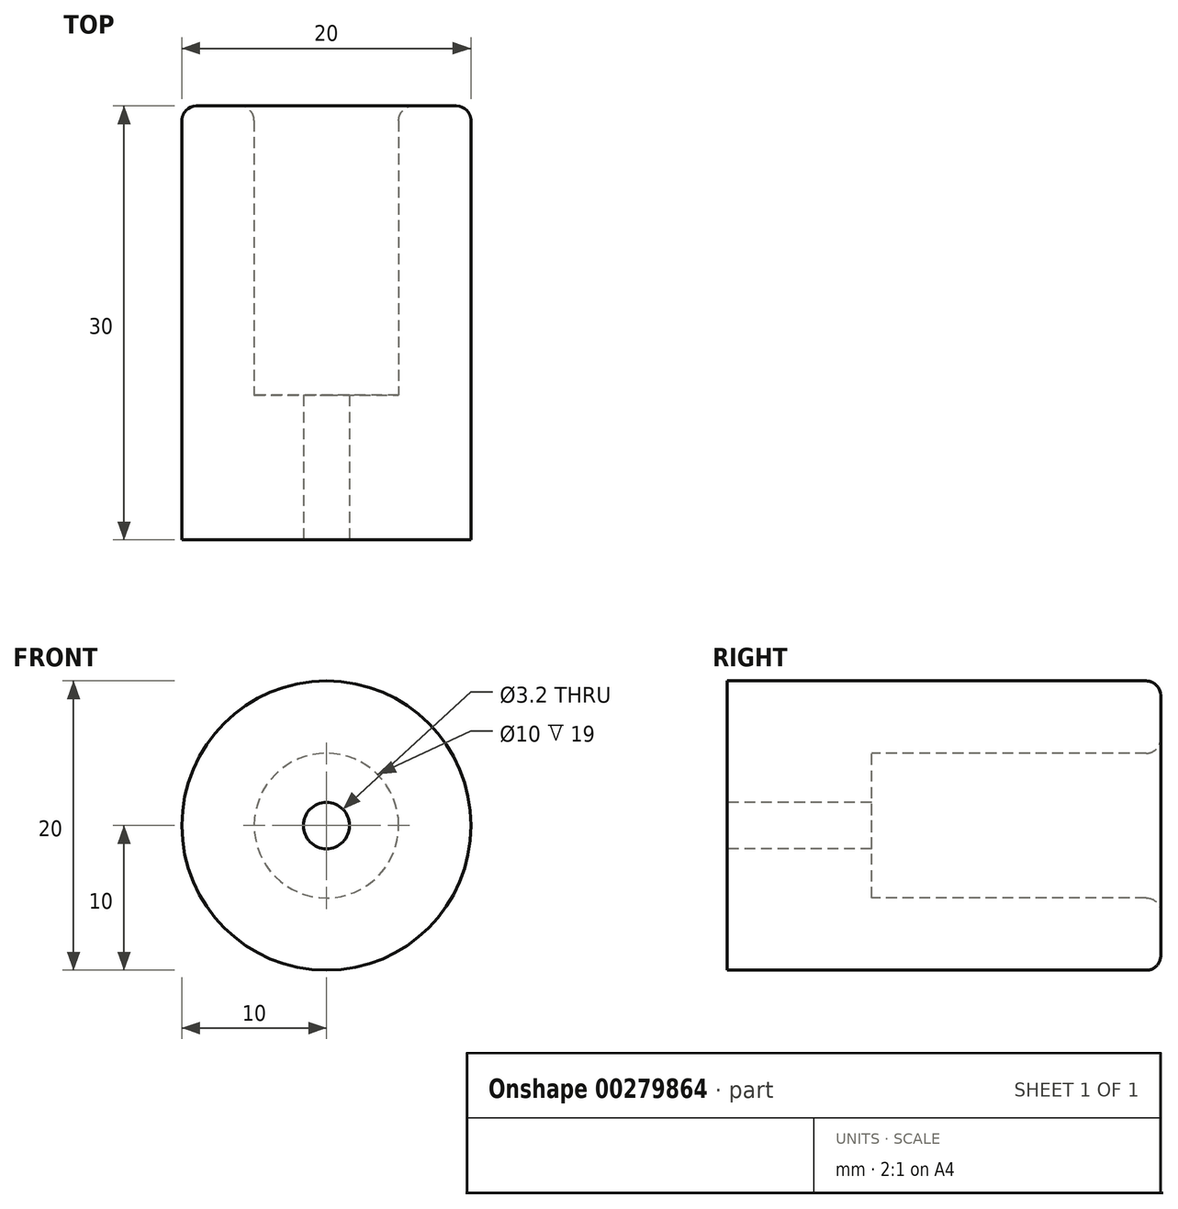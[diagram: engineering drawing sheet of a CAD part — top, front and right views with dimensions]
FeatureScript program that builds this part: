
annotation { "Feature Type Name" : "Feature", "Feature Type Description" : "" }
export const myFeature = defineFeature(function(context is Context, id is Id, definition is map)
    precondition{}
    {
        {
            var Q0;
            Q0=qCreatedBy(makeId("Top.planeOp"),FACE);
            var sketch = newSketch(context, id + "F0", { "sketchPlane" : qUnion([Q0])});
            skLineSegment(sketch, "E0", {"start": v(-1.6, 0) * mm, "end": v(-10, 0) * mm});
            skLineSegment(sketch, "E1", {"start": v(-10, 0) * mm, "end": v(-10, 29) * mm});
            skLineSegment(sketch, "E2", {"start": v(-9, 30) * mm, "end": v(-6, 30) * mm});
            skLineSegment(sketch, "E3", {"start": v(-5, 29) * mm, "end": v(-5, 10) * mm});
            skLineSegment(sketch, "E4", {"start": v(-5, 10) * mm, "end": v(-1.6, 10) * mm});
            skLineSegment(sketch, "E5", {"start": v(-1.6, 10) * mm, "end": v(-1.6, 0) * mm});
            skLineSegment(sketch, "E6", {"start": v(0, 0) * mm, "end": v(0, 11.74) * mm, "construction": true});
            skPoint(sketch, "E7.visualSharp", {"position": v(-10, 30) * mm});
            skArc(sketch, "E7.filletArc", {"start": v(-9, 30) * mm, "mid": v(-9.7, 29.7) * mm, "end": v(-10, 29) * mm});
            skPoint(sketch, "E8.visualSharp", {"position": v(-5, 30) * mm});
            skArc(sketch, "E8.filletArc", {"start": v(-5, 29) * mm, "mid": v(-5.3, 29.7) * mm, "end": v(-6, 30) * mm});
            skSolve(sketch);
        }
        {
            var Q0;
            Q0 = qSketchRegion(id + "F0", true);
            var Q1;
            Q1=sQuery(id+"F0.wireOp",EDGE,"E6");
            revolve(context, id + "F1", {"entities" : qUnion([Q0]), "axis" : qUnion([Q1]), "revolveType" : RevolveType.FULL});
        }
    });
